# Revit family: Boiling Water System-Rheem-Lazer Commercial
name_source: partatom
category: Mechanical Equipment
revit_build: Autodesk Revit 2017 (Build: 20160225_1515(x64)
units: mm (PartAtom-declared; Revit-internal decimal feet)

## family parameters
Cut with Voids When Loaded = No
Host = Face
OmniClass Number = 23.65.35.11.14
OmniClass Title = Instantaneous Water Heaters
Part Type = Normal
Room Calculation Point = No
Round Connector Dimension = Use Radius
Shared = No

## types (13) — shared parameters
Assembly Code = D3020100
Connector Radius = 8 mm  [stored 0.0262467 ft]
Default Elevation = 1200 mm
Description = The Rheem Lazer is a very clever option with sleek but understated appearance and space saving over bench installation
Keynote = HWU
Manufacturer = Rheem Australia Pty Ltd
Outlet Base Offset = 58 mm  [stored 0.190289 ft]
URL = http://www.rheem.com.au

## per-type parameters (varying)
| type | Apparent Load | Commercial | Depth_ANZRS | Economy | Height_ANZRS | Material_ANZRS | Model | Outlet Position | Type Comments | Width_ANZRS |
| Lazer with Eco Button - 7.5L - White | 2400 VA | No | 191 mm  [stored 0.62664 ft] | Yes | 515 mm  [stored 1.68963 ft] | Metal-Powdercoat-White-Rheem | 70307W | 269 mm  [stored 0.882546 ft] | Initial delivery 50 cups with recovery 123 cups per hour | 334 mm  [stored 1.0958 ft] |
| Lazer with Eco Button - 5L - White | 2400 VA | No | 191 mm  [stored 0.62664 ft] | Yes | 465 mm  [stored 1.52559 ft] | Metal-Powdercoat-White-Rheem | 70305W | 269 mm  [stored 0.882546 ft] | Initial delivery 35 cups with recovery 123 cups per hour | 334 mm  [stored 1.0958 ft] |
| Lazer with Eco Button - 3L - White | 1800 VA | No | 158 mm  [stored 0.518373 ft] | Yes | 435 mm  [stored 1.42717 ft] | Metal-Powdercoat-White-Rheem | 70303W | 236 mm | Initial delivery 20 cups with recovery 102 cups per hour | 283 mm  [stored 0.928478 ft] |
| Lazer with Timer - 40L - Stainless Steel | 4600 VA | Yes | 340 mm  [stored 1.11549 ft] | No | 615 mm  [stored 2.01772 ft] | Metal-Stainless Steel-Brushed-Rheem | 70240S | 418 mm  [stored 1.37139 ft] | Initial delivery 42 litres with recovery 41 litres per hour | 490 mm  [stored 1.60761 ft] |
| Lazer with Timer - 40L - White | 4600 VA | Yes | 340 mm  [stored 1.11549 ft] | No | 615 mm  [stored 2.01772 ft] | Metal-Powdercoat-White-Rheem | 70240W | 418 mm  [stored 1.37139 ft] | Initial delivery 42 litres with recovery 41 litres per hour | 490 mm  [stored 1.60761 ft] |
| Lazer with Timer - 25L - White | 3600 VA | Yes | 299 mm  [stored 0.980971 ft] | No | 720 mm  [stored 2.3622 ft] | Metal-Powdercoat-White-Rheem | 70225W | 377 mm  [stored 1.23688 ft] | Initial delivery 27 litres with recovery 33 litres per hour | 334 mm  [stored 1.0958 ft] |
| Lazer with Timer - 25L - Stainless Steel | 3600 VA | Yes | 299 mm  [stored 0.980971 ft] | No | 720 mm  [stored 2.3622 ft] | Metal-Stainless Steel-Brushed-Rheem | 70225S | 377 mm  [stored 1.23688 ft] | Initial delivery 27 litres with recovery 33 litres per hour | 334 mm  [stored 1.0958 ft] |
| Lazer with Timer - 15L - Stainless Steel | 2400 VA | Yes | 299 mm  [stored 0.980971 ft] | No | 515 mm  [stored 1.68963 ft] | Metal-Stainless Steel-Brushed-Rheem | 70215S | 377 mm  [stored 1.23688 ft] | Initial delivery 17 litres with recovery 21 litres per hour | 334 mm  [stored 1.0958 ft] |
| Lazer with Timer - 15L - White | 2400 VA | Yes | 299 mm  [stored 0.980971 ft] | No | 515 mm  [stored 1.68963 ft] | Metal-Powdercoat-White-Rheem | 70215W | 377 mm  [stored 1.23688 ft] | Initial delivery 17 litres with recovery 21 litres per hour | 334 mm  [stored 1.0958 ft] |
| Lazer with Timer - 10L - White | 2400 VA | Yes | 191 mm  [stored 0.62664 ft] | No | 615 mm  [stored 2.01772 ft] | Metal-Powdercoat-White-Rheem | 70210W | 269 mm  [stored 0.882546 ft] | Initial delivery 11 litres with recovery 21 litres per hour | 334 mm  [stored 1.0958 ft] |
| Lazer with Timer - 10L - Stainless Steel | 2400 VA | Yes | 191 mm  [stored 0.62664 ft] | No | 615 mm  [stored 2.01772 ft] | Metal-Stainless Steel-Brushed-Rheem | 70210S | 269 mm  [stored 0.882546 ft] | Initial delivery 11 litres with recovery 21 litres per hour | 334 mm  [stored 1.0958 ft] |
| Lazer with Timer - 7.5L - Stainless Steel | 2400 VA | Yes | 191 mm  [stored 0.62664 ft] | No | 515 mm  [stored 1.68963 ft] | Metal-Stainless Steel-Brushed-Rheem | 70207S | 269 mm  [stored 0.882546 ft] | Initial delivery 8.5 litres with recovery 21 litres per hour | 334 mm  [stored 1.0958 ft] |
| Lazer with Timer - 7.5L - White | 2400 VA | Yes | 191 mm  [stored 0.62664 ft] | No | 515 mm  [stored 1.68963 ft] | Metal-Powdercoat-White-Rheem | 70207W | 269 mm  [stored 0.882546 ft] | Initial delivery 8.5 litres with recovery 21 litres per hour | 334 mm  [stored 1.0958 ft] |

note: [stored X ft] marks values corroborated as IEEE doubles in the binary element streams (Revit-internal decimal feet)

## geometry (parser evidence)
native form markers: Blend x20, Sweep x3
no freeform markers — native parametric forms only
